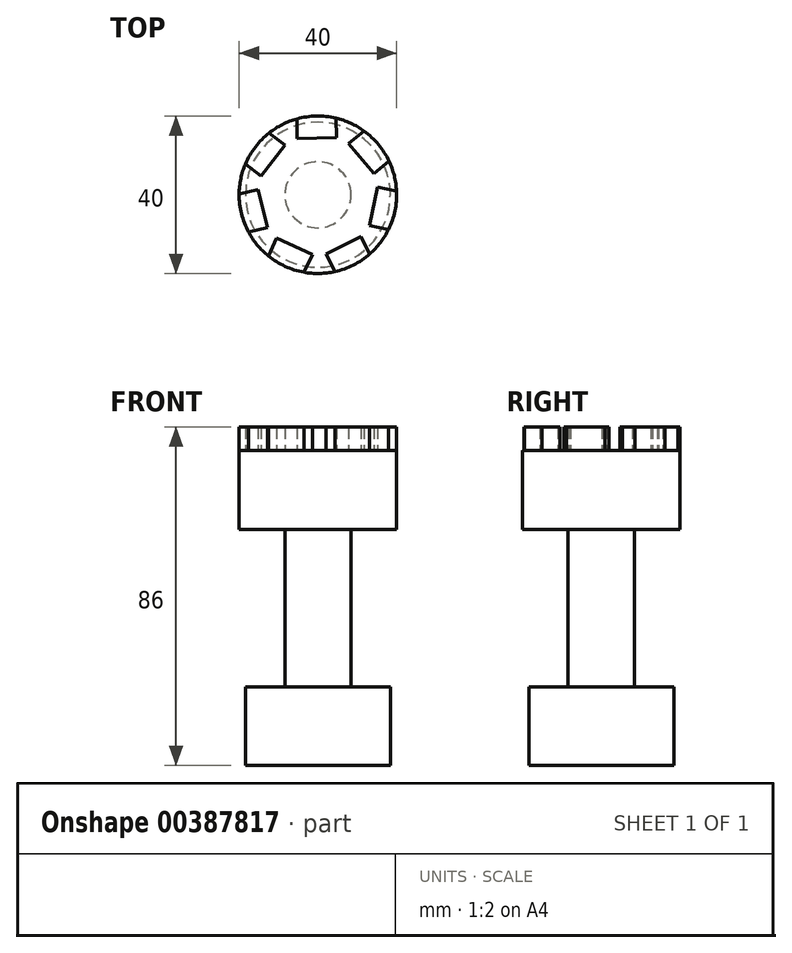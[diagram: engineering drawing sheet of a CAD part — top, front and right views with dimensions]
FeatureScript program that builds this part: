
annotation { "Feature Type Name" : "Feature", "Feature Type Description" : "" }
export const myFeature = defineFeature(function(context is Context, id is Id, definition is map)
    precondition{}
    {
        {
            var Q0;
            Q0=qCreatedBy(makeId("Front.planeOp"),FACE);
            var sketch = newSketch(context, id + "F0", { "sketchPlane" : qUnion([Q0])});
            skLineSegment(sketch, "E0", {"start": v(0, 107.27) * mm, "end": v(0, -118.54) * mm, "construction": true});
            skLineSegment(sketch, "E1", {"start": v(0, 40) * mm, "end": v(0, -40) * mm});
            skLineSegment(sketch, "E2", {"start": v(0, -40) * mm, "end": v(18.4, -40) * mm});
            skLineSegment(sketch, "E3", {"start": v(18.4, -40) * mm, "end": v(18.4, -20) * mm});
            skLineSegment(sketch, "E4", {"start": v(18.4, -20) * mm, "end": v(8.4, -20) * mm});
            skLineSegment(sketch, "E5", {"start": v(8.4, -20) * mm, "end": v(8.4, 20) * mm});
            skLineSegment(sketch, "E6", {"start": v(8.4, 20) * mm, "end": v(20, 20) * mm});
            skLineSegment(sketch, "E7", {"start": v(20, 20) * mm, "end": v(20, 40) * mm});
            skLineSegment(sketch, "E8", {"start": v(20, 40) * mm, "end": v(0, 40) * mm});
            skSolve(sketch);
        }
        {
            var Q0;
            Q0 = qSketchRegion(id + "F0", true);
            var Q1;
            Q1=sQuery(id+"F0.wireOp",EDGE,"E0");
            revolve(context, id + "F1", {"entities" : qUnion([Q0]), "axis" : qUnion([Q1]), "revolveType" : RevolveType.FULL});
        }
        {
            var Q0;
            Q0=makeQuery(id+"F1.opRevolve","SWEPT_FACE",FACE,{"disambiguationData":[OSD([sQuery(id+"F0.wireOp",EDGE,"E8")])]});
            var sketch = newSketch(context, id + "F2", { "sketchPlane" : qUnion([Q0])});
            skLineSegment(sketch, "E9", {"start": v(-5.32, 19.28) * mm, "end": v(-5.32, 14.28) * mm});
            skLineSegment(sketch, "E10", {"start": v(-5.32, 14.28) * mm, "end": v(4.68, 14.47) * mm});
            skLineSegment(sketch, "E11", {"start": v(4.68, 14.47) * mm, "end": v(4.58, 19.47) * mm});
            skCircle(sketch, "E12", {"center": v(0, 0) * mm, "radius": 20.07 * mm});
            skArc(sketch, "E13", {"start": v(4.58, 19.47) * mm, "mid": v(-0.38, 20) * mm, "end": v(-5.32, 19.28) * mm});
            skSolve(sketch);
        }
        {
            var Q0;
            Q0=makeQuery(id+"F2.imprint","IMPRINT",FACE,{"disambiguationData":[TD([[makeQuery(id+"F2.imprint","IMPRINT",EDGE,{"derivedFrom":sQuery(id+"F2.wireOp",EDGE,"E9")}),1.0]])]});
            extrude(context, id + "F3", {"entities" : qUnion([Q0]), "operationType" : NewBodyOperationType.ADD, "depth" : 6 * mm});
        }
        {
            var Q0;
            Q0=makeQuery(id+"F1.opRevolve","SWEPT_BODY",BODY,{"disambiguationData":[OSD([sQuery(id+"F0.wireOp",EDGE,"E1"),sQuery(id+"F0.wireOp",EDGE,"E2"),sQuery(id+"F0.wireOp",EDGE,"E3"),sQuery(id+"F0.wireOp",EDGE,"E4"),sQuery(id+"F0.wireOp",EDGE,"E5"),sQuery(id+"F0.wireOp",EDGE,"E6"),sQuery(id+"F0.wireOp",EDGE,"E7"),sQuery(id+"F0.wireOp",EDGE,"E8")])]});
            var Q1;
            Q1=makeQuery(id+"F3.boolean.opBoolean","MERGE",FACE,{"derivedFrom":[makeQuery(id+"F1.opRevolve","SWEPT_FACE",FACE,{"disambiguationData":[OSD([sQuery(id+"F0.wireOp",EDGE,"E7")])]}),makeQuery(id+"F3.opExtrude","SWEPT_FACE",FACE,{"disambiguationData":[OSD([sQuery(id+"F2.wireOp",EDGE,"E13")])]})]});
            circularPattern(context, id + "F4", {"entities" : qUnion([Q0]), "axis" : qUnion([Q1]), "angle" : 360 * degree, "instanceCount" : 7, "equalSpace" : true});
        }
    });
